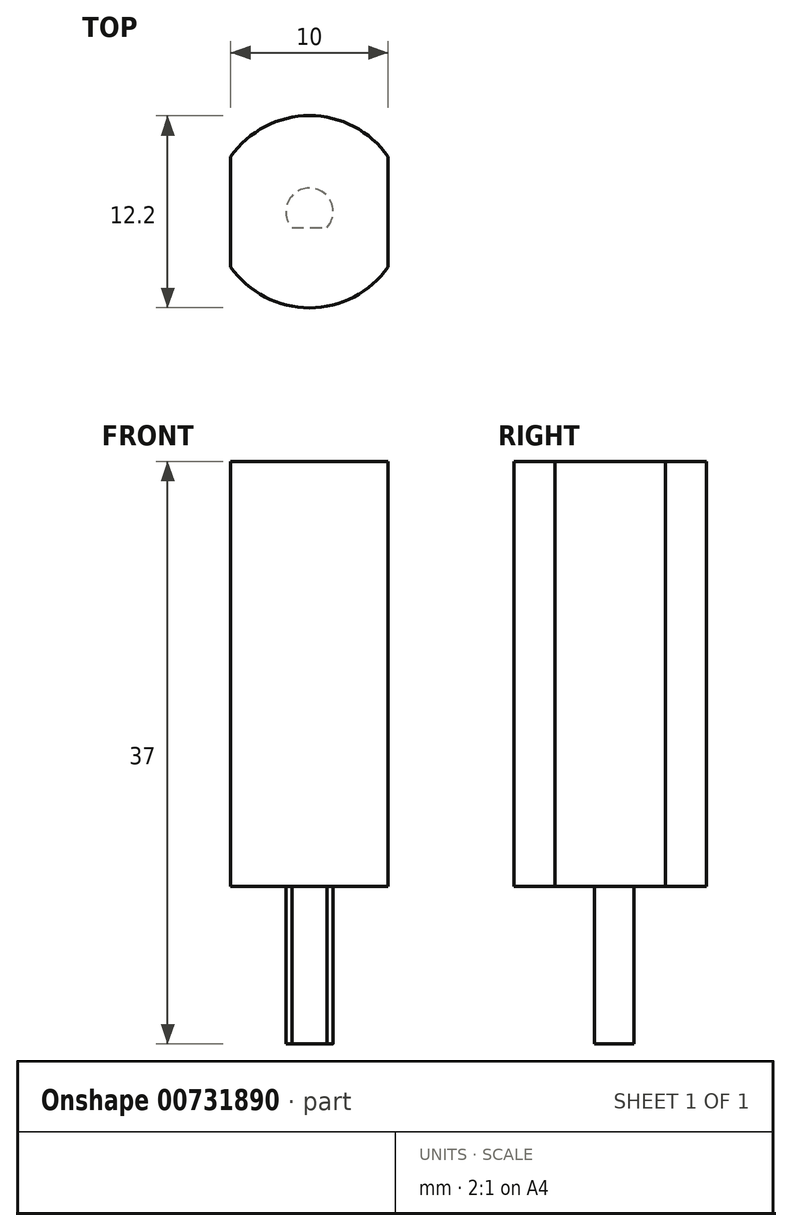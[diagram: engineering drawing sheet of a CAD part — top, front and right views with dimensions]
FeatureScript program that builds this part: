
annotation { "Feature Type Name" : "Feature", "Feature Type Description" : "" }
export const myFeature = defineFeature(function(context is Context, id is Id, definition is map)
    precondition{}
    {
        {
            var Q0;
            Q0=qCreatedBy(makeId("Top.planeOp"),FACE);
            var sketch = newSketch(context, id + "F0", { "sketchPlane" : qUnion([Q0])});
            skArc(sketch, "E0", {"start": v(5, 3.5) * mm, "mid": v(0, 6.1) * mm, "end": v(-5, 3.5) * mm});
            skLineSegment(sketch, "E1", {"start": v(-5, 3.5) * mm, "end": v(-5, -3.5) * mm});
            skLineSegment(sketch, "E2", {"start": v(5, 3.5) * mm, "end": v(5, -3.5) * mm});
            skPoint(sketch, "E3.end.orphan", {"position": v(5, 0) * mm});
            skPoint(sketch, "E4.end.orphan", {"position": v(-5, 0) * mm});
            skArc(sketch, "E5.trimOffspring", {"start": v(-5, -3.5) * mm, "mid": v(0, -6.1) * mm, "end": v(5, -3.5) * mm});
            skSolve(sketch);
        }
        {
            var Q0;
            Q0=makeQuery(id+"F0.imprint","IMPRINT",FACE,{"disambiguationData":[TD([[makeQuery(id+"F0.imprint","IMPRINT",EDGE,{"derivedFrom":sQuery(id+"F0.wireOp",EDGE,"E0")}),1.0]])]});
            var sketch = newSketch(context, id + "F1", { "sketchPlane" : qUnion([Q0])});
            skArc(sketch, "E6", {"start": v(1.12, -1) * mm, "mid": v(0, 1.5) * mm, "end": v(-1.12, -1) * mm});
            skLineSegment(sketch, "E7", {"start": v(-1.12, -1) * mm, "end": v(1.12, -1) * mm});
            skPoint(sketch, "E8.orphan", {"position": v(0, 1.5) * mm});
            skPoint(sketch, "E9.end.orphan", {"position": v(0, -1) * mm});
            skSolve(sketch);
        }
        {
            var Q0;
            Q0=makeQuery(id+"F0.imprint","IMPRINT",FACE,{"disambiguationData":[TD([[makeQuery(id+"F0.imprint","IMPRINT",EDGE,{"derivedFrom":sQuery(id+"F0.wireOp",EDGE,"E0")}),1.0]])]});
            extrude(context, id + "F2", {"entities" : qUnion([Q0]), "depth" : 27 * mm, "offsetDistance" : 25 * mm});
        }
        {
            var Q0;
            Q0=makeQuery(id+"F1.imprint","IMPRINT",FACE,{"disambiguationData":[TD([[makeQuery(id+"F1.imprint","IMPRINT",EDGE,{"derivedFrom":sQuery(id+"F1.wireOp",EDGE,"E6")}),1.0]])]});
            extrude(context, id + "F3", {"entities" : qUnion([Q0]), "operationType" : NewBodyOperationType.ADD, "oppositeDirection" : true, "depth" : 10 * mm, "offsetDistance" : 25 * mm});
        }
    });
